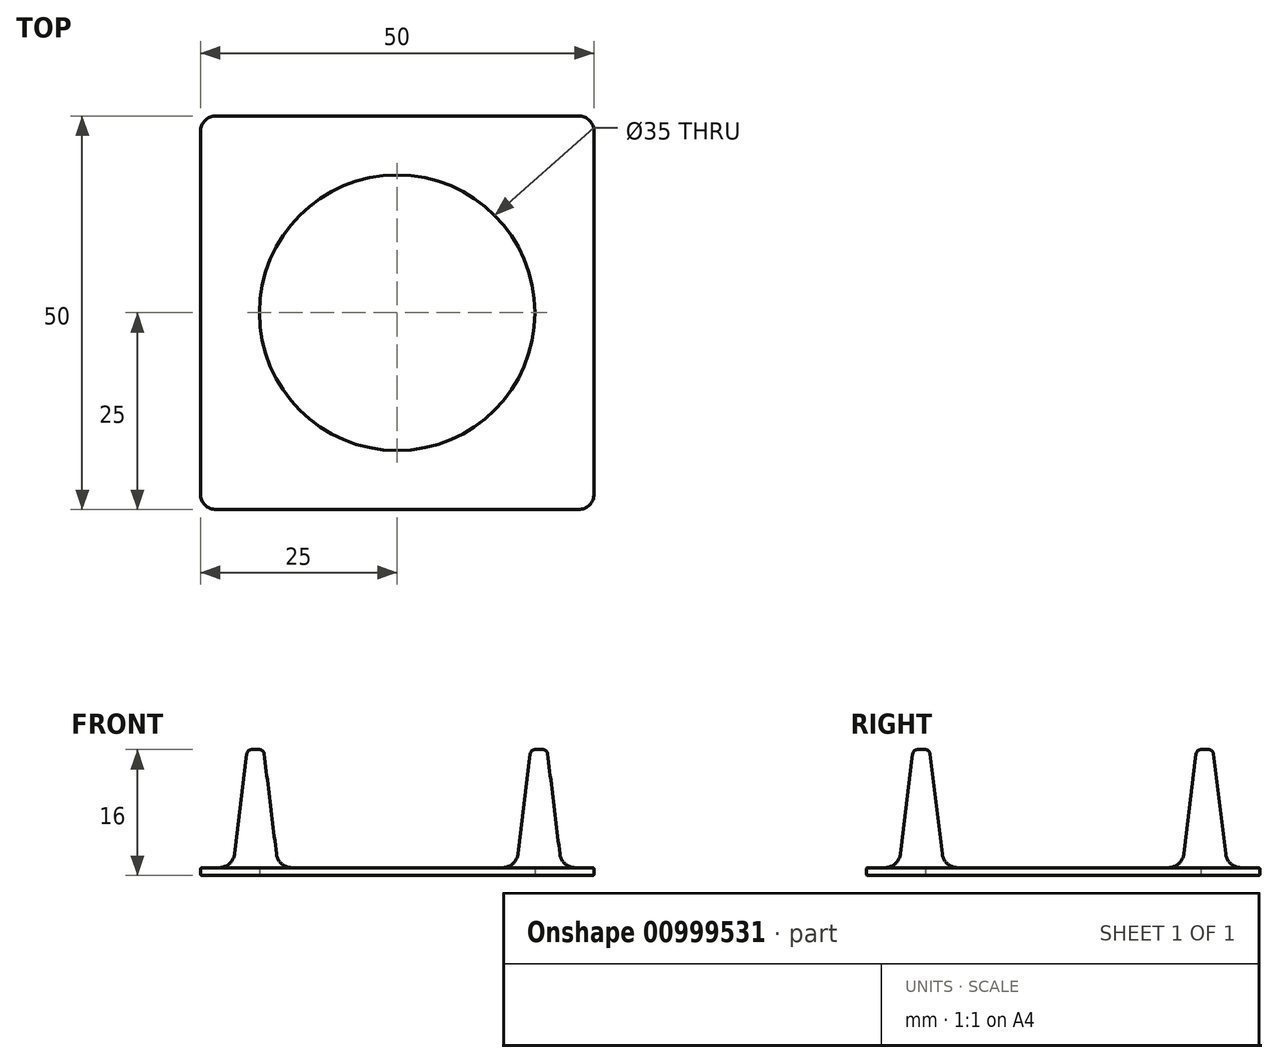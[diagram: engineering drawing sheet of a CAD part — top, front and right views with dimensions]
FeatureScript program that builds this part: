
annotation { "Feature Type Name" : "Feature", "Feature Type Description" : "" }
export const myFeature = defineFeature(function(context is Context, id is Id, definition is map)
    precondition{}
    {
        {
            var Q0;
            Q0=qCreatedBy(makeId("Top.planeOp"),FACE);
            var sketch = newSketch(context, id + "F0", { "sketchPlane" : qUnion([Q0])});
            skLineSegment(sketch, "E0.bottom", {"start": v(25, 25) * mm, "end": v(-25, 25) * mm});
            skLineSegment(sketch, "E0.top", {"start": v(25, -25) * mm, "end": v(-25, -25) * mm});
            skLineSegment(sketch, "E0.left", {"start": v(25, 25) * mm, "end": v(25, -25) * mm});
            skLineSegment(sketch, "E0.right", {"start": v(-25, 25) * mm, "end": v(-25, -25) * mm});
            skPoint(sketch, "E0.middle", {"position": v(0, 0) * mm});
            skCircle(sketch, "E1", {"center": v(0, 0) * mm, "radius": 17.5 * mm});
            skCircle(sketch, "E2", {"center": v(-18, 18) * mm, "radius": 3 * mm});
            skCircle(sketch, "E3.0.1.0", {"center": v(-18, -18) * mm, "radius": 3 * mm});
            skCircle(sketch, "E3.1.0.0", {"center": v(18, 18) * mm, "radius": 3 * mm});
            skCircle(sketch, "E3.1.1.0", {"center": v(18, -18) * mm, "radius": 3 * mm});
            skLineSegment(sketch, "E3.direction1", {"start": v(-18, 18) * mm, "end": v(18, 18) * mm, "construction": true});
            skLineSegment(sketch, "E3.direction2", {"start": v(-18, 18) * mm, "end": v(-18, -18) * mm, "construction": true});
            skSolve(sketch);
        }
        {
            var Q0;
            Q0=makeQuery(id+"F0.imprint","IMPRINT",FACE,{"disambiguationData":[TD([[makeQuery(id+"F0.imprint","IMPRINT",EDGE,{"derivedFrom":sQuery(id+"F0.wireOp",EDGE,"E2")}),1.0]])]});
            var Q1;
            Q1=makeQuery(id+"F0.imprint","IMPRINT",FACE,{"disambiguationData":[TD([[makeQuery(id+"F0.imprint","IMPRINT",EDGE,{"derivedFrom":sQuery(id+"F0.wireOp",EDGE,"E3.0.1.0")}),1.0]])]});
            var Q2;
            Q2=makeQuery(id+"F0.imprint","IMPRINT",FACE,{"disambiguationData":[TD([[makeQuery(id+"F0.imprint","IMPRINT",EDGE,{"derivedFrom":sQuery(id+"F0.wireOp",EDGE,"E3.1.1.0")}),1.0]])]});
            var Q3;
            Q3=makeQuery(id+"F0.imprint","IMPRINT",FACE,{"disambiguationData":[TD([[makeQuery(id+"F0.imprint","IMPRINT",EDGE,{"derivedFrom":sQuery(id+"F0.wireOp",EDGE,"E3.1.0.0")}),1.0]])]});
            var Q4;
            Q4=makeQuery(id+"F0.imprint","IMPRINT",FACE,{"disambiguationData":[TD([[makeQuery(id+"F0.imprint","IMPRINT",EDGE,{"derivedFrom":sQuery(id+"F0.wireOp",EDGE,"E0.bottom")}),1.0]])]});
            extrude(context, id + "F1", {"entities" : qUnion([Q0, Q1, Q2, Q3, Q4]), "depth" : 1 * mm, "offsetDistance" : 25 * mm});
        }
        {
            var Q0;
            Q0=makeQuery(id+"F1.opExtrude","SWEPT_EDGE",EDGE,{"disambiguationData":[OSD([sQuery(id+"F0.wireOp",EDGE,"E0.top"),sQuery(id+"F0.wireOp",EDGE,"E0.right")])]});
            var Q1;
            Q1=makeQuery(id+"F1.opExtrude","SWEPT_EDGE",EDGE,{"disambiguationData":[OSD([sQuery(id+"F0.wireOp",EDGE,"E0.top"),sQuery(id+"F0.wireOp",EDGE,"E0.left")])]});
            var Q2;
            Q2=makeQuery(id+"F1.opExtrude","SWEPT_EDGE",EDGE,{"disambiguationData":[OSD([sQuery(id+"F0.wireOp",EDGE,"E0.bottom"),sQuery(id+"F0.wireOp",EDGE,"E0.left")])]});
            var Q3;
            Q3=makeQuery(id+"F1.opExtrude","SWEPT_EDGE",EDGE,{"disambiguationData":[OSD([sQuery(id+"F0.wireOp",EDGE,"E0.bottom"),sQuery(id+"F0.wireOp",EDGE,"E0.right")])]});
            fillet(context, id + "F2", {"entities" : qUnion([Q0, Q1, Q2, Q3]), "radius" : 2 * mm, "tangentPropagation" : true, "allowEdgeOverflow" : false});
        }
        {
            var Q0;
            Q0=makeQuery(id+"F0.imprint","IMPRINT",FACE,{"disambiguationData":[TD([[makeQuery(id+"F0.imprint","IMPRINT",EDGE,{"derivedFrom":sQuery(id+"F0.wireOp",EDGE,"E3.0.1.0")}),1.0]])]});
            var Q1;
            Q1=makeQuery(id+"F0.imprint","IMPRINT",FACE,{"disambiguationData":[TD([[makeQuery(id+"F0.imprint","IMPRINT",EDGE,{"derivedFrom":sQuery(id+"F0.wireOp",EDGE,"E2")}),1.0]])]});
            var Q2;
            Q2=makeQuery(id+"F0.imprint","IMPRINT",FACE,{"disambiguationData":[TD([[makeQuery(id+"F0.imprint","IMPRINT",EDGE,{"derivedFrom":sQuery(id+"F0.wireOp",EDGE,"E3.1.0.0")}),1.0]])]});
            var Q3;
            Q3=makeQuery(id+"F0.imprint","IMPRINT",FACE,{"disambiguationData":[TD([[makeQuery(id+"F0.imprint","IMPRINT",EDGE,{"derivedFrom":sQuery(id+"F0.wireOp",EDGE,"E3.1.1.0")}),1.0]])]});
            extrude(context, id + "F3", {"entities" : qUnion([Q0, Q1, Q2, Q3]), "operationType" : NewBodyOperationType.ADD, "depth" : (1 + 15) * mm, "offsetDistance" : 25 * mm, "hasDraft" : true, "draftAngle" : 7 * degree, "draftPullDirection" : true});
        }
        {
            var Q0;
            Q0=makeQuery(id+"F1.opExtrude","CAP_FACE",FACE,{"disambiguationData":[OSD([sQuery(id+"F0.wireOp",EDGE,"E0.bottom"),sQuery(id+"F0.wireOp",EDGE,"E0.top"),sQuery(id+"F0.wireOp",EDGE,"E0.left"),sQuery(id+"F0.wireOp",EDGE,"E0.right"),sQuery(id+"F0.wireOp",EDGE,"E1")])],"isStart":true});
            var Q1;
            Q1=makeQuery(id+"F1.opExtrude","CAP_EDGE",EDGE,{"disambiguationData":[OSD([sQuery(id+"F0.wireOp",EDGE,"E1")])],"isStart":false});
            var Q2;
            Q2=makeQuery(id+"F1.opExtrude","CAP_EDGE",EDGE,{"disambiguationData":[OSD([sQuery(id+"F0.wireOp",EDGE,"E0.top")])],"isStart":false});
            fillet(context, id + "F4", {"entities" : qUnion([Q0, Q1, Q2]), "radius" : 0.2 * mm, "tangentPropagation" : true, "allowEdgeOverflow" : false});
        }
        {
            var Q0;
            Q0=makeQuery(id+"F3.opExtrude","CAP_EDGE",EDGE,{"disambiguationData":[OSD([sQuery(id+"F0.wireOp",EDGE,"E2")])],"isStart":false});
            var Q1;
            Q1=makeQuery(id+"F3.opExtrude","CAP_EDGE",EDGE,{"disambiguationData":[OSD([sQuery(id+"F0.wireOp",EDGE,"E3.0.1.0")])],"isStart":false});
            var Q2;
            Q2=makeQuery(id+"F3.opExtrude","CAP_EDGE",EDGE,{"disambiguationData":[OSD([sQuery(id+"F0.wireOp",EDGE,"E3.1.1.0")])],"isStart":false});
            var Q3;
            Q3=makeQuery(id+"F3.opExtrude","CAP_EDGE",EDGE,{"disambiguationData":[OSD([sQuery(id+"F0.wireOp",EDGE,"E3.1.0.0")])],"isStart":false});
            fillet(context, id + "F5", {"entities" : qUnion([Q0, Q1, Q2, Q3]), "radius" : 0.6 * mm, "tangentPropagation" : true, "allowEdgeOverflow" : false});
        }
        {
            var Q0;
            Q0=makeQuery(id+"F3.boolean.opBoolean","INTERSECT",EDGE,{"derivedFrom":[makeQuery(id+"F1.opExtrude","CAP_FACE",FACE,{"disambiguationData":[OSD([sQuery(id+"F0.wireOp",EDGE,"E0.bottom"),sQuery(id+"F0.wireOp",EDGE,"E0.top"),sQuery(id+"F0.wireOp",EDGE,"E0.left"),sQuery(id+"F0.wireOp",EDGE,"E0.right"),sQuery(id+"F0.wireOp",EDGE,"E1")])],"isStart":false}),makeQuery(id+"F3.opExtrude","SWEPT_FACE",FACE,{"disambiguationData":[OSD([sQuery(id+"F0.wireOp",EDGE,"E2")])]})]});
            var Q1;
            Q1=makeQuery(id+"F3.boolean.opBoolean","INTERSECT",EDGE,{"derivedFrom":[makeQuery(id+"F1.opExtrude","CAP_FACE",FACE,{"disambiguationData":[OSD([sQuery(id+"F0.wireOp",EDGE,"E0.bottom"),sQuery(id+"F0.wireOp",EDGE,"E0.top"),sQuery(id+"F0.wireOp",EDGE,"E0.left"),sQuery(id+"F0.wireOp",EDGE,"E0.right"),sQuery(id+"F0.wireOp",EDGE,"E1")])],"isStart":false}),makeQuery(id+"F3.opExtrude","SWEPT_FACE",FACE,{"disambiguationData":[OSD([sQuery(id+"F0.wireOp",EDGE,"E3.0.1.0")])]})]});
            var Q2;
            Q2=makeQuery(id+"F3.boolean.opBoolean","INTERSECT",EDGE,{"derivedFrom":[makeQuery(id+"F1.opExtrude","CAP_FACE",FACE,{"disambiguationData":[OSD([sQuery(id+"F0.wireOp",EDGE,"E0.bottom"),sQuery(id+"F0.wireOp",EDGE,"E0.top"),sQuery(id+"F0.wireOp",EDGE,"E0.left"),sQuery(id+"F0.wireOp",EDGE,"E0.right"),sQuery(id+"F0.wireOp",EDGE,"E1")])],"isStart":false}),makeQuery(id+"F3.opExtrude","SWEPT_FACE",FACE,{"disambiguationData":[OSD([sQuery(id+"F0.wireOp",EDGE,"E3.1.1.0")])]})]});
            var Q3;
            Q3=makeQuery(id+"F3.boolean.opBoolean","INTERSECT",EDGE,{"derivedFrom":[makeQuery(id+"F1.opExtrude","CAP_FACE",FACE,{"disambiguationData":[OSD([sQuery(id+"F0.wireOp",EDGE,"E0.bottom"),sQuery(id+"F0.wireOp",EDGE,"E0.top"),sQuery(id+"F0.wireOp",EDGE,"E0.left"),sQuery(id+"F0.wireOp",EDGE,"E0.right"),sQuery(id+"F0.wireOp",EDGE,"E1")])],"isStart":false}),makeQuery(id+"F3.opExtrude","SWEPT_FACE",FACE,{"disambiguationData":[OSD([sQuery(id+"F0.wireOp",EDGE,"E3.1.0.0")])]})]});
            fillet(context, id + "F6", {"entities" : qUnion([Q0, Q1, Q2, Q3]), "radius" : 2 * mm, "tangentPropagation" : true, "allowEdgeOverflow" : false});
        }
    });
